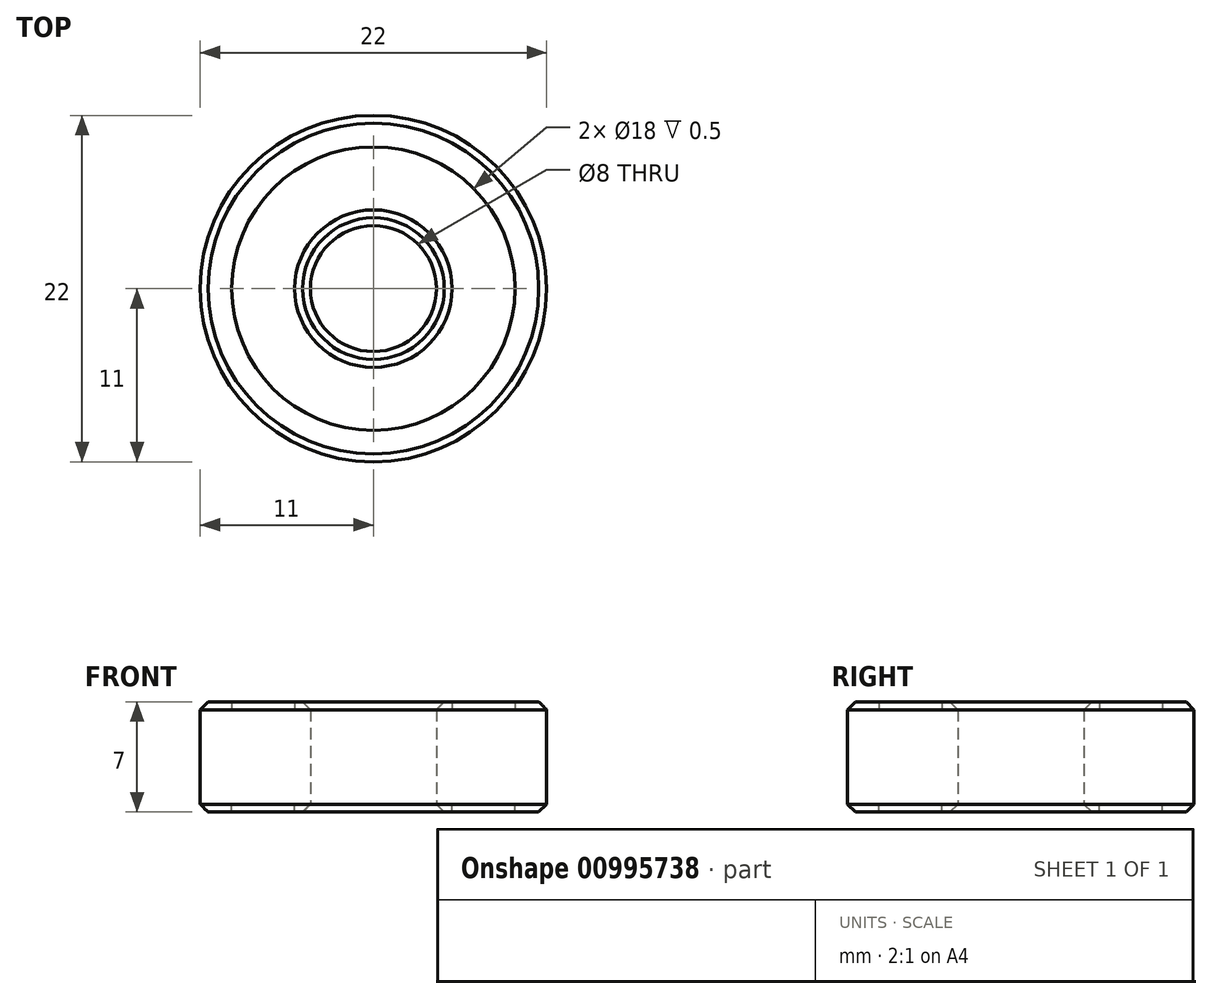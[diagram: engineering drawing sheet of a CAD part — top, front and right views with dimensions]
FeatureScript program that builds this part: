
annotation { "Feature Type Name" : "Feature", "Feature Type Description" : "" }
export const myFeature = defineFeature(function(context is Context, id is Id, definition is map)
    precondition{}
    {
        {
            var Q0;
            Q0=qCreatedBy(makeId("Front.planeOp"),FACE);
            var sketch = newSketch(context, id + "F0", { "sketchPlane" : qUnion([Q0])});
            skLineSegment(sketch, "E0", {"start": v(4, 3.5) * mm, "end": v(4, 0) * mm});
            skLineSegment(sketch, "E1", {"start": v(4, 0) * mm, "end": v(11, 0) * mm});
            skLineSegment(sketch, "E2", {"start": v(11, 0) * mm, "end": v(11, 3.5) * mm});
            skLineSegment(sketch, "E3", {"start": v(11, 3.5) * mm, "end": v(9, 3.5) * mm});
            skLineSegment(sketch, "E4", {"start": v(9, 3.5) * mm, "end": v(9, 3) * mm});
            skLineSegment(sketch, "E5", {"start": v(9, 3) * mm, "end": v(5, 3) * mm});
            skLineSegment(sketch, "E6", {"start": v(5, 3) * mm, "end": v(5, 3.5) * mm});
            skLineSegment(sketch, "E7", {"start": v(5, 3.5) * mm, "end": v(4, 3.5) * mm});
            skLineSegment(sketch, "E8", {"start": v(0, 0) * mm, "end": v(0, 6.25) * mm, "construction": true});
            skSolve(sketch);
        }
        {
            var Q0;
            Q0=makeQuery(id+"F0.imprint","IMPRINT",FACE,{"disambiguationData":[TD([[makeQuery(id+"F0.imprint","IMPRINT",EDGE,{"derivedFrom":sQuery(id+"F0.wireOp",EDGE,"E0")}),1.0]])]});
            var Q1;
            Q1=sQuery(id+"F0.wireOp",EDGE,"E8");
            revolve(context, id + "F1", {"surfaceOperationType" : NewSurfaceOperationType.NEW, "entities" : qUnion([Q0]), "axis" : qUnion([Q1]), "revolveType" : RevolveType.FULL});
        }
        {
            var Q0;
            Q0=makeQuery(id+"F1.opRevolve","SWEPT_BODY",BODY,{"disambiguationData":[OSD([sQuery(id+"F0.wireOp",EDGE,"E0"),sQuery(id+"F0.wireOp",EDGE,"E1"),sQuery(id+"F0.wireOp",EDGE,"E2"),sQuery(id+"F0.wireOp",EDGE,"E3"),sQuery(id+"F0.wireOp",EDGE,"E4"),sQuery(id+"F0.wireOp",EDGE,"E5"),sQuery(id+"F0.wireOp",EDGE,"E6"),sQuery(id+"F0.wireOp",EDGE,"E7")])]});
            var Q1;
            Q1=qCreatedBy(makeId("Top.planeOp"),FACE);
            mirror(context, id + "F2", {"operationType" : NewBodyOperationType.ADD, "entities" : qUnion([Q0]), "mirrorPlane" : qUnion([Q1])});
        }
        {
            var Q0;
            Q0=makeQuery(id+"F1.opRevolve","SWEPT_EDGE",EDGE,{"disambiguationData":[OSD([sQuery(id+"F0.wireOp",EDGE,"E2"),sQuery(id+"F0.wireOp",EDGE,"E3")])]});
            var Q1;
            Q1=makeQuery(id+"F2.opPattern","COPY",EDGE,{"derivedFrom":makeQuery(id+"F1.opRevolve","SWEPT_EDGE",EDGE,{"disambiguationData":[OSD([sQuery(id+"F0.wireOp",EDGE,"E2"),sQuery(id+"F0.wireOp",EDGE,"E3")])]}),"instanceName":"1"});
            var Q2;
            Q2=makeQuery(id+"F1.opRevolve","SWEPT_EDGE",EDGE,{"disambiguationData":[OSD([sQuery(id+"F0.wireOp",EDGE,"E0"),sQuery(id+"F0.wireOp",EDGE,"E7")])]});
            var Q3;
            Q3=makeQuery(id+"F2.opPattern","COPY",EDGE,{"derivedFrom":makeQuery(id+"F1.opRevolve","SWEPT_EDGE",EDGE,{"disambiguationData":[OSD([sQuery(id+"F0.wireOp",EDGE,"E0"),sQuery(id+"F0.wireOp",EDGE,"E7")])]}),"instanceName":"1"});
            chamfer(context, id + "F3", {"entities" : qUnion([Q0, Q1, Q2, Q3]), "width" : 0.5 * mm, "tangentPropagation" : true});
        }
    });
